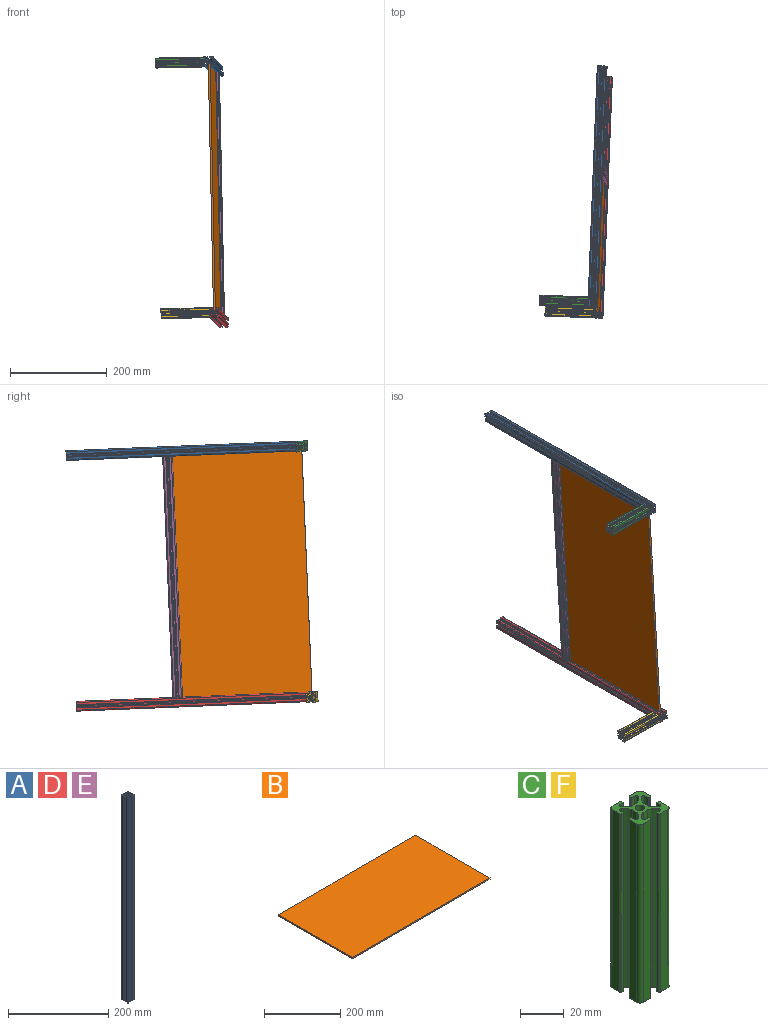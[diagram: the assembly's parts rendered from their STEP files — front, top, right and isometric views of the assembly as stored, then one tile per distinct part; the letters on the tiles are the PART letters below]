
ASSEMBLY  parts=6 mates=10
PART A: 75 faces, bbox 20x20x500 mm
  f0: plane 500x0.7mm, normal (0,1,0), area 350mm2, adj f1,f72,f73,f74
  f1: cylinder r=0.8mm len=500mm, axis (0,0,-1), area 628.3mm2, adj f0,f2,f73,f74
  f2: plane 500x4.7mm, normal (-1,0,0), area 2350mm2, adj f1,f3,f73,f74
  f3: cylinder r=2mm len=500mm, axis (0,0,-1), area 1570.8mm2, adj f2,f4,f73,f74
  f4: plane 500x4.7mm, normal (0,-1,0), area 2350mm2, adj f3,f5,f73,f74
  f5: cylinder r=0.8mm len=500mm, axis (0,0,-1), area 628.3mm2, adj f4,f6,f73,f74
  f6: plane 500x0.7mm, normal (1,0,0), area 350mm2, adj f5,f7,f73,f74
  f7: cylinder r=0.3mm len=500mm, axis (0,0,-1), area 235.6mm2, adj f6,f8,f73,f74
  f8: plane 500x2.12mm, normal (0,1,0), area 1058.8mm2, adj f7,f9,f73,f74
  f9: cylinder r=0.83mm len=500mm, axis (0,0,-1), area 980.7mm2, adj f8,f10,f73,f74
  f10: plane 500x2.25mm, normal (0.71,-0.71,0), area 1591.2mm2, adj f9,f11,f73,f74
  f11: cylinder r=3mm len=500mm, axis (0,0,-1), area 1178.1mm2, adj f10,f12,f73,f74
  f12: plane 500x2.27mm, normal (0,-1,0), area 1134.6mm2, adj f11,f13,f73,f74
  f13: cylinder r=3mm len=500mm, axis (0,0,-1), area 1178.1mm2, adj f12,f14,f73,f74
  f14: plane 500x2.25mm, normal (-0.71,-0.71,0), area 1591.2mm2, adj f13,f15,f73,f74
  f15: cylinder r=0.83mm len=500mm, axis (0,0,-1), area 980.7mm2, adj f14,f16,f73,f74
  f16: plane 500x2.12mm, normal (0,1,0), area 1058.8mm2, adj f15,f17,f73,f74
  f17: cylinder r=0.3mm len=500mm, axis (0,0,-1), area 235.6mm2, adj f16,f18,f73,f74
  f18: plane 500x0.7mm, normal (-1,0,0), area 350mm2, adj f17,f19,f73,f74
  f19: cylinder r=0.8mm len=500mm, axis (0,0,-1), area 628.3mm2, adj f18,f20,f73,f74
  f20: plane 500x4.7mm, normal (0,-1,0), area 2350mm2, adj f19,f21,f73,f74
  f21: cylinder r=2mm len=500mm, axis (0,0,-1), area 1570.8mm2, adj f20,f22,f73,f74
  f22: plane 500x4.7mm, normal (1,0,0), area 2350mm2, adj f21,f23,f73,f74
  f23: cylinder r=0.8mm len=500mm, axis (0,0,-1), area 628.3mm2, adj f22,f24,f73,f74
  f24: plane 500x0.7mm, normal (0,1,0), area 350mm2, adj f23,f25,f73,f74
  f25: cylinder r=0.3mm len=500mm, axis (0,0,-1), area 235.6mm2, adj f24,f26,f73,f74
  f26: plane 500x2.12mm, normal (-1,0,0), area 1058.8mm2, adj f25,f27,f73,f74
  f27: cylinder r=0.83mm len=500mm, axis (0,0,-1), area 980.7mm2, adj f26,f28,f73,f74
  f28: plane 500x2.25mm, normal (0.71,0.71,0), area 1591.2mm2, adj f27,f29,f73,f74
  f29: cylinder r=3mm len=500mm, axis (0,0,-1), area 1178.1mm2, adj f28,f30,f73,f74
  f30: plane 500x2.27mm, normal (1,0,0), area 1134.6mm2, adj f29,f31,f73,f74
  f31: cylinder r=3mm len=500mm, axis (0,0,-1), area 1178.1mm2, adj f30,f32,f73,f74
  f32: plane 500x2.25mm, normal (0.71,-0.71,0), area 1591.2mm2, adj f31,f33,f73,f74
  f33: cylinder r=0.83mm len=500mm, axis (0,0,-1), area 980.7mm2, adj f32,f34,f73,f74
  f34: plane 500x2.12mm, normal (-1,0,0), area 1058.8mm2, adj f33,f35,f73,f74
  f35: cylinder r=0.3mm len=500mm, axis (0,0,-1), area 235.6mm2, adj f34,f36,f73,f74
  f36: plane 500x0.7mm, normal (0,-1,0), area 350mm2, adj f35,f37,f73,f74
  f37: cylinder r=0.8mm len=500mm, axis (0,0,-1), area 628.3mm2, adj f36,f38,f73,f74
  f38: plane 500x4.7mm, normal (1,0,0), area 2350mm2, adj f37,f39,f73,f74
  f39: cylinder r=2mm len=500mm, axis (0,0,-1), area 1570.8mm2, adj f38,f40,f73,f74
  f40: plane 500x4.7mm, normal (0,1,0), area 2350mm2, adj f39,f41,f73,f74
  f41: cylinder r=0.8mm len=500mm, axis (0,0,-1), area 628.3mm2, adj f40,f42,f73,f74
  f42: plane 500x0.7mm, normal (-1,0,0), area 350mm2, adj f41,f43,f73,f74
  f43: cylinder r=0.3mm len=500mm, axis (0,0,-1), area 235.6mm2, adj f42,f44,f73,f74
  f44: plane 500x2.12mm, normal (0,-1,0), area 1058.8mm2, adj f43,f45,f73,f74
  f45: cylinder r=0.83mm len=500mm, axis (0,0,-1), area 980.7mm2, adj f44,f46,f73,f74
  f46: plane 500x2.25mm, normal (-0.71,0.71,0), area 1591.2mm2, adj f45,f47,f73,f74
  f47: cylinder r=3mm len=500mm, axis (0,0,-1), area 1178.1mm2, adj f46,f48,f73,f74
  f48: plane 500x2.27mm, normal (0,1,0), area 1134.6mm2, adj f47,f49,f73,f74
  f49: cylinder r=3mm len=500mm, axis (0,0,-1), area 1178.1mm2, adj f48,f50,f73,f74
  f50: plane 500x2.25mm, normal (0.71,0.71,0), area 1591.2mm2, adj f49,f51,f73,f74
  f51: cylinder r=0.83mm len=500mm, axis (0,0,-1), area 980.7mm2, adj f50,f52,f73,f74
  f52: plane 500x2.12mm, normal (0,-1,0), area 1058.8mm2, adj f51,f53,f73,f74
  f53: cylinder r=0.3mm len=500mm, axis (0,0,-1), area 235.6mm2, adj f52,f54,f73,f74
  f54: plane 500x0.7mm, normal (1,0,0), area 350mm2, adj f53,f55,f73,f74
  f55: cylinder r=0.8mm len=500mm, axis (0,0,-1), area 628.3mm2, adj f54,f56,f73,f74
  f56: plane 500x4.7mm, normal (0,1,0), area 2350mm2, adj f55,f57,f73,f74
  f57: cylinder r=2mm len=500mm, axis (0,0,-1), area 1570.8mm2, adj f56,f58,f73,f74
  f58: plane 500x4.7mm, normal (-1,0,0), area 2350mm2, adj f57,f59,f73,f74
  f59: cylinder r=0.8mm len=500mm, axis (0,0,-1), area 628.3mm2, adj f58,f60,f73,f74
  f60: plane 500x0.7mm, normal (0,-1,0), area 350mm2, adj f59,f61,f73,f74
  f61: cylinder r=0.3mm len=500mm, axis (0,0,-1), area 235.6mm2, adj f60,f62,f73,f74
  f62: plane 500x2.12mm, normal (1,0,0), area 1058.8mm2, adj f61,f63,f73,f74
  f63: cylinder r=0.83mm len=500mm, axis (0,0,-1), area 980.7mm2, adj f62,f64,f73,f74
  f64: plane 500x2.25mm, normal (-0.71,-0.71,0), area 1591.2mm2, adj f63,f65,f73,f74
  f65: cylinder r=3mm len=500mm, axis (0,0,-1), area 1178.1mm2, adj f64,f66,f73,f74
  f66: plane 500x2.27mm, normal (-1,0,0), area 1134.6mm2, adj f65,f67,f73,f74
  f67: cylinder r=3mm len=500mm, axis (0,0,-1), area 1178.1mm2, adj f66,f68,f73,f74
  f68: plane 500x2.25mm, normal (-0.71,0.71,0), area 1591.2mm2, adj f67,f69,f73,f74
  f69: cylinder r=0.83mm len=500mm, axis (0,0,-1), area 980.7mm2, adj f68,f70,f73,f74
  f70: plane 500x2.12mm, normal (1,0,0), area 1058.8mm2, adj f69,f72,f73,f74
  f71: cylinder r=2.15mm len=500mm, axis (0,0,-1), area 6754.4mm2, adj f73,f74
  f72: cylinder r=0.3mm len=500mm, axis (0,0,-1), area 235.6mm2, adj f0,f70,f73,f74
  f73: plane 20x20mm, normal (0,0,1), area 183.9mm2, adj f0,f1,f2,f3,f4,f5,f6,f7
  f74: plane 20x20mm, normal (0,0,-1), area 183.9mm2, adj f0,f1,f2,f3,f4,f5,f6,f7
PART B: 6 faces, bbox 512x275x4 mm
  f0: plane 512x275mm, normal (0,0,-1), area 140800mm2, adj f1,f2,f3,f4
  f1: plane 275x4mm, normal (1,0,0), area 1100mm2, adj f0,f2,f4,f5
  f2: plane 512x4mm, normal (0,1,0), area 2048mm2, adj f0,f1,f3,f5
  f3: plane 275x4mm, normal (-1,0,0), area 1100mm2, adj f0,f2,f4,f5
  f4: plane 512x4mm, normal (0,-1,0), area 2048mm2, adj f0,f1,f3,f5
  f5: plane 512x275mm, normal (0,0,1), area 140800mm2, adj f1,f2,f3,f4
PART C: 75 faces, bbox 20x20x100 mm
  f0: plane 100x0.7mm, normal (0,1,0), area 70mm2, adj f1,f72,f73,f74
  f1: cylinder r=0.8mm len=100mm, axis (0,0,-1), area 125.7mm2, adj f0,f2,f73,f74
  f2: plane 100x4.7mm, normal (-1,0,0), area 470mm2, adj f1,f3,f73,f74
  f3: cylinder r=2mm len=100mm, axis (0,0,-1), area 314.2mm2, adj f2,f4,f73,f74
  f4: plane 100x4.7mm, normal (0,-1,0), area 470mm2, adj f3,f5,f73,f74
  f5: cylinder r=0.8mm len=100mm, axis (0,0,-1), area 125.7mm2, adj f4,f6,f73,f74
  f6: plane 100x0.7mm, normal (1,0,0), area 70mm2, adj f5,f7,f73,f74
  f7: cylinder r=0.3mm len=100mm, axis (0,0,-1), area 47.1mm2, adj f6,f8,f73,f74
  f8: plane 100x2.12mm, normal (0,1,0), area 211.8mm2, adj f7,f9,f73,f74
  f9: cylinder r=0.83mm len=100mm, axis (0,0,-1), area 196.1mm2, adj f8,f10,f73,f74
  f10: plane 100x2.25mm, normal (0.71,-0.71,0), area 318.2mm2, adj f9,f11,f73,f74
  f11: cylinder r=3mm len=100mm, axis (0,0,-1), area 235.6mm2, adj f10,f12,f73,f74
  f12: plane 100x2.27mm, normal (0,-1,0), area 226.9mm2, adj f11,f13,f73,f74
  f13: cylinder r=3mm len=100mm, axis (0,0,-1), area 235.6mm2, adj f12,f14,f73,f74
  f14: plane 100x2.25mm, normal (-0.71,-0.71,0), area 318.2mm2, adj f13,f15,f73,f74
  f15: cylinder r=0.83mm len=100mm, axis (0,0,-1), area 196.1mm2, adj f14,f16,f73,f74
  f16: plane 100x2.12mm, normal (0,1,0), area 211.8mm2, adj f15,f17,f73,f74
  f17: cylinder r=0.3mm len=100mm, axis (0,0,-1), area 47.1mm2, adj f16,f18,f73,f74
  f18: plane 100x0.7mm, normal (-1,0,0), area 70mm2, adj f17,f19,f73,f74
  f19: cylinder r=0.8mm len=100mm, axis (0,0,-1), area 125.7mm2, adj f18,f20,f73,f74
  f20: plane 100x4.7mm, normal (0,-1,0), area 470mm2, adj f19,f21,f73,f74
  f21: cylinder r=2mm len=100mm, axis (0,0,-1), area 314.2mm2, adj f20,f22,f73,f74
  f22: plane 100x4.7mm, normal (1,0,0), area 470mm2, adj f21,f23,f73,f74
  f23: cylinder r=0.8mm len=100mm, axis (0,0,-1), area 125.7mm2, adj f22,f24,f73,f74
  f24: plane 100x0.7mm, normal (0,1,0), area 70mm2, adj f23,f25,f73,f74
  f25: cylinder r=0.3mm len=100mm, axis (0,0,-1), area 47.1mm2, adj f24,f26,f73,f74
  f26: plane 100x2.12mm, normal (-1,0,0), area 211.8mm2, adj f25,f27,f73,f74
  f27: cylinder r=0.83mm len=100mm, axis (0,0,-1), area 196.1mm2, adj f26,f28,f73,f74
  f28: plane 100x2.25mm, normal (0.71,0.71,0), area 318.2mm2, adj f27,f29,f73,f74
  f29: cylinder r=3mm len=100mm, axis (0,0,-1), area 235.6mm2, adj f28,f30,f73,f74
  f30: plane 100x2.27mm, normal (1,0,0), area 226.9mm2, adj f29,f31,f73,f74
  f31: cylinder r=3mm len=100mm, axis (0,0,-1), area 235.6mm2, adj f30,f32,f73,f74
  f32: plane 100x2.25mm, normal (0.71,-0.71,0), area 318.2mm2, adj f31,f33,f73,f74
  f33: cylinder r=0.83mm len=100mm, axis (0,0,-1), area 196.1mm2, adj f32,f34,f73,f74
  f34: plane 100x2.12mm, normal (-1,0,0), area 211.8mm2, adj f33,f35,f73,f74
  f35: cylinder r=0.3mm len=100mm, axis (0,0,-1), area 47.1mm2, adj f34,f36,f73,f74
  f36: plane 100x0.7mm, normal (0,-1,0), area 70mm2, adj f35,f37,f73,f74
  f37: cylinder r=0.8mm len=100mm, axis (0,0,-1), area 125.7mm2, adj f36,f38,f73,f74
  f38: plane 100x4.7mm, normal (1,0,0), area 470mm2, adj f37,f39,f73,f74
  f39: cylinder r=2mm len=100mm, axis (0,0,-1), area 314.2mm2, adj f38,f40,f73,f74
  f40: plane 100x4.7mm, normal (0,1,0), area 470mm2, adj f39,f41,f73,f74
  f41: cylinder r=0.8mm len=100mm, axis (0,0,-1), area 125.7mm2, adj f40,f42,f73,f74
  f42: plane 100x0.7mm, normal (-1,0,0), area 70mm2, adj f41,f43,f73,f74
  f43: cylinder r=0.3mm len=100mm, axis (0,0,-1), area 47.1mm2, adj f42,f44,f73,f74
  f44: plane 100x2.12mm, normal (0,-1,0), area 211.8mm2, adj f43,f45,f73,f74
  f45: cylinder r=0.83mm len=100mm, axis (0,0,-1), area 196.1mm2, adj f44,f46,f73,f74
  f46: plane 100x2.25mm, normal (-0.71,0.71,0), area 318.2mm2, adj f45,f47,f73,f74
  f47: cylinder r=3mm len=100mm, axis (0,0,-1), area 235.6mm2, adj f46,f48,f73,f74
  f48: plane 100x2.27mm, normal (0,1,0), area 226.9mm2, adj f47,f49,f73,f74
  f49: cylinder r=3mm len=100mm, axis (0,0,-1), area 235.6mm2, adj f48,f50,f73,f74
  f50: plane 100x2.25mm, normal (0.71,0.71,0), area 318.2mm2, adj f49,f51,f73,f74
  f51: cylinder r=0.83mm len=100mm, axis (0,0,-1), area 196.1mm2, adj f50,f52,f73,f74
  f52: plane 100x2.12mm, normal (0,-1,0), area 211.8mm2, adj f51,f53,f73,f74
  f53: cylinder r=0.3mm len=100mm, axis (0,0,-1), area 47.1mm2, adj f52,f54,f73,f74
  f54: plane 100x0.7mm, normal (1,0,0), area 70mm2, adj f53,f55,f73,f74
  f55: cylinder r=0.8mm len=100mm, axis (0,0,-1), area 125.7mm2, adj f54,f56,f73,f74
  f56: plane 100x4.7mm, normal (0,1,0), area 470mm2, adj f55,f57,f73,f74
  f57: cylinder r=2mm len=100mm, axis (0,0,-1), area 314.2mm2, adj f56,f58,f73,f74
  f58: plane 100x4.7mm, normal (-1,0,0), area 470mm2, adj f57,f59,f73,f74
  f59: cylinder r=0.8mm len=100mm, axis (0,0,-1), area 125.7mm2, adj f58,f60,f73,f74
  f60: plane 100x0.7mm, normal (0,-1,0), area 70mm2, adj f59,f61,f73,f74
  f61: cylinder r=0.3mm len=100mm, axis (0,0,-1), area 47.1mm2, adj f60,f62,f73,f74
  f62: plane 100x2.12mm, normal (1,0,0), area 211.8mm2, adj f61,f63,f73,f74
  f63: cylinder r=0.83mm len=100mm, axis (0,0,-1), area 196.1mm2, adj f62,f64,f73,f74
  f64: plane 100x2.25mm, normal (-0.71,-0.71,0), area 318.2mm2, adj f63,f65,f73,f74
  f65: cylinder r=3mm len=100mm, axis (0,0,-1), area 235.6mm2, adj f64,f66,f73,f74
  f66: plane 100x2.27mm, normal (-1,0,0), area 226.9mm2, adj f65,f67,f73,f74
  f67: cylinder r=3mm len=100mm, axis (0,0,-1), area 235.6mm2, adj f66,f68,f73,f74
  f68: plane 100x2.25mm, normal (-0.71,0.71,0), area 318.2mm2, adj f67,f69,f73,f74
  f69: cylinder r=0.83mm len=100mm, axis (0,0,-1), area 196.1mm2, adj f68,f70,f73,f74
  f70: plane 100x2.12mm, normal (1,0,0), area 211.8mm2, adj f69,f72,f73,f74
  f71: cylinder r=2.15mm len=100mm, axis (0,0,-1), area 1350.9mm2, adj f73,f74
  f72: cylinder r=0.3mm len=100mm, axis (0,0,-1), area 47.1mm2, adj f0,f70,f73,f74
  f73: plane 20x20mm, normal (0,0,1), area 183.9mm2, adj f0,f1,f2,f3,f4,f5,f6,f7
  f74: plane 20x20mm, normal (0,0,-1), area 183.9mm2, adj f0,f1,f2,f3,f4,f5,f6,f7
PART D: same geometry as A
PART E: same geometry as A
PART F: same geometry as C
PLACE A rot(axis=(-0.02,-0.69,0.72),179.3deg) t=(1.03,682.23,562.65)mm
PLACE B rot(axis=(-0.04,-1,0),91.3deg) t=(-4.79,320.8,317.05)mm
PLACE C rot(axis=(0.7,0,0.71),176.7deg) t=(-128.13,197.26,580.4)mm
PLACE D rot(axis=(-0.02,-0.69,0.72),179.3deg) t=(12,660.45,43.22)mm
PLACE E rot(axis=(0.72,0.69,-0.01),177.4deg) t=(-6.88,472.3,561.28)mm
PLACE F rot(axis=(0.7,0,0.71),176.7deg) t=(-117.16,175.47,60.97)mm
MATE planar D.f38 <-> F.f3  axis (-1,0.04,-0.02) through (-7.71,411,47.61)mm
MATE planar D.f20 <-> E.f39  axis (-0.02,0.04,1) through (-3.69,411.49,63.34)mm
MATE planar B.f2 <-> E.f66  axis (0.04,1,-0.04) through (-1.38,458.15,311.36)mm
MATE planar B.f0 <-> D.f6  axis (1,-0.04,0.02) through (-4.79,320.8,317.05)mm
MATE planar F.f40 <-> D.f71  axis (-0.04,-1,0.04) through (-67.73,163.8,68.16)mm
MATE planar C.f40 <-> A.f3  axis (-0.04,-1,0.04) through (-78.7,185.59,587.59)mm
MATE planar B.f0 <-> A.f54  axis (1,-0.04,0.02) through (-4.79,320.8,317.05)mm
MATE planar C.f71 <-> A.f22  axis (1,-0.04,0.02) through (-28.23,193.42,582.67)mm
MATE planar A.f40 <-> E.f3  axis (0.02,-0.04,-1) through (-14.24,432.44,562.79)mm
MATE planar D.f12 <-> B.f3  axis (-0.02,0.04,1) through (2.09,411,57.13)mm
